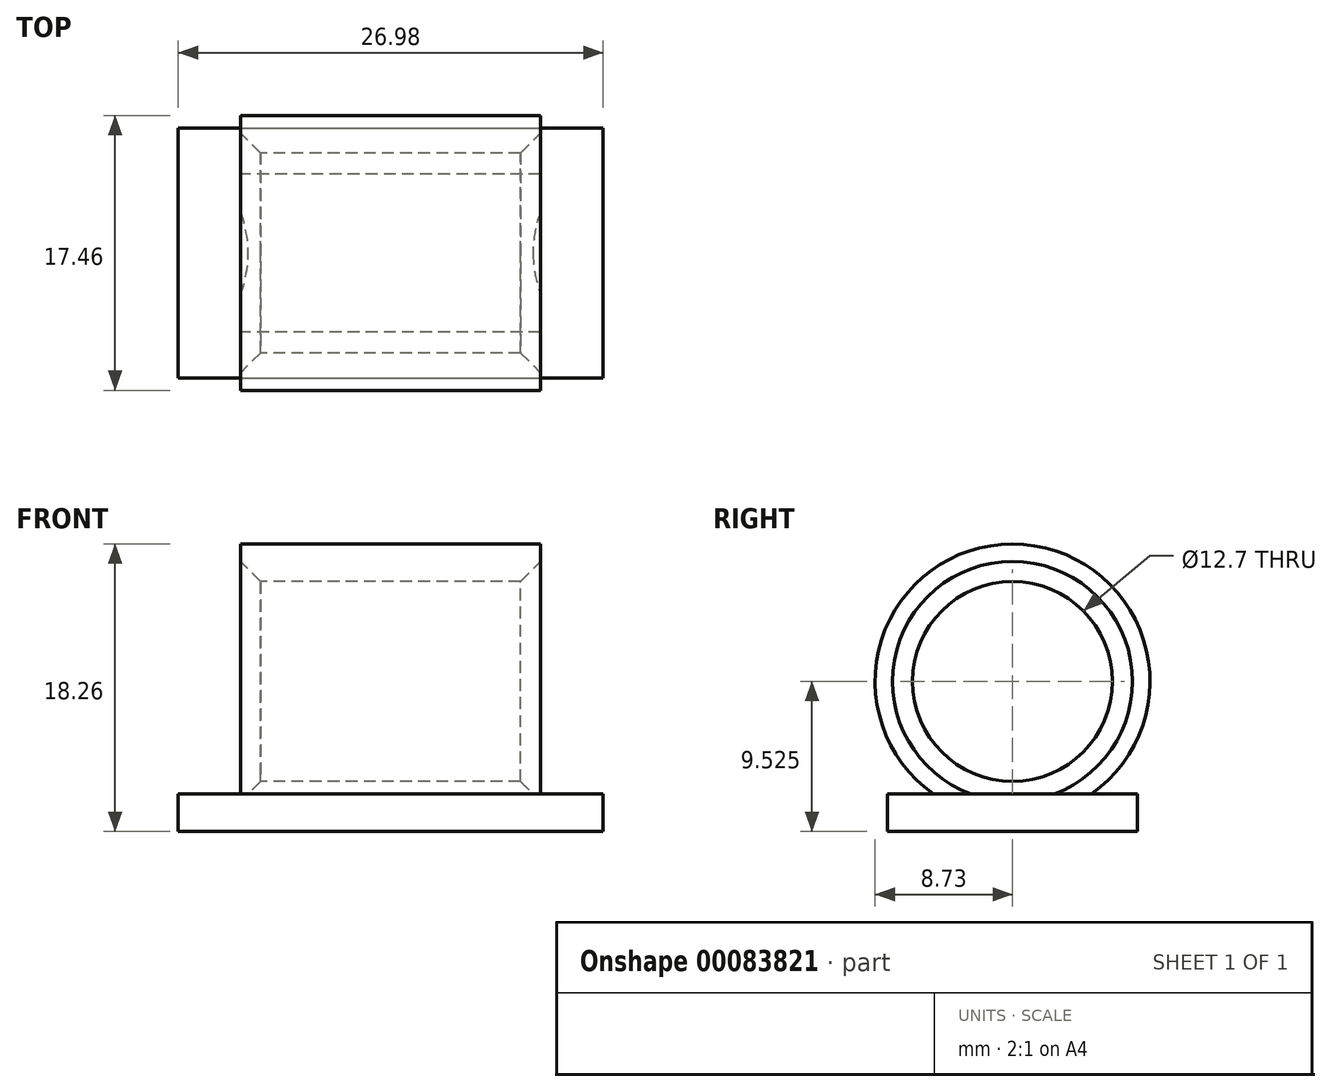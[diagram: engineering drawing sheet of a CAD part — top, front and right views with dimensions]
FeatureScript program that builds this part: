
annotation { "Feature Type Name" : "Feature", "Feature Type Description" : "" }
export const myFeature = defineFeature(function(context is Context, id is Id, definition is map)
    precondition{}
    {
        {
            var Q0;
            Q0=qCreatedBy(makeId("Top.planeOp"),FACE);
            var sketch = newSketch(context, id + "F0", { "sketchPlane" : qUnion([Q0])});
            skLineSegment(sketch, "E0.bottom", {"start": v(-13.5, 7.94) * mm, "end": v(13.5, 7.94) * mm});
            skLineSegment(sketch, "E0.top", {"start": v(-13.5, -7.94) * mm, "end": v(13.5, -7.94) * mm});
            skLineSegment(sketch, "E0.left", {"start": v(-13.5, 7.94) * mm, "end": v(-13.5, -7.94) * mm});
            skLineSegment(sketch, "E0.right", {"start": v(13.5, 7.94) * mm, "end": v(13.5, -7.94) * mm});
            skSolve(sketch);
        }
        {
            var Q0;
            Q0=makeQuery(id+"F0.imprint","IMPRINT",FACE,{"disambiguationData":[TD([[makeQuery(id+"F0.imprint","IMPRINT",EDGE,{"derivedFrom":sQuery(id+"F0.wireOp",EDGE,"E0.bottom")}),-1.0]])]});
            extrude(context, id + "F1", {"entities" : qUnion([Q0]), "depth" : 2.38 * mm});
        }
        {
            var Q0;
            Q0=qCreatedBy(makeId("Right.planeOp"),FACE);
            var sketch = newSketch(context, id + "F2", { "sketchPlane" : qUnion([Q0])});
            skCircle(sketch, "E1", {"center": v(0, 9.53) * mm, "radius": 6.35 * mm});
            skCircle(sketch, "E2", {"center": v(0, 9.53) * mm, "radius": 8.73 * mm});
            skLineSegment(sketch, "E3.0", {"start": v(7.94, 2.38) * mm, "end": v(-7.94, 2.38) * mm});
            skSolve(sketch);
        }
        {
            var Q0;
            Q0=makeQuery(id+"F2.imprint","IMPRINT",FACE,{"disambiguationData":[TD([[makeQuery(id+"F2.imprint","IMPRINT",EDGE,{"derivedFrom":sQuery(id+"F2.wireOp",EDGE,"E1")}),-1.0]])]});
            extrude(context, id + "F3", {"entities" : qUnion([Q0]), "operationType" : NewBodyOperationType.ADD, "endBound" : BoundingType.SYMMETRIC, "depth" : 19.05 * mm});
        }
        {
            var Q0;
            Q0=makeQuery(id+"F3.opExtrude","CAP_EDGE",EDGE,{"disambiguationData":[OSD([sQuery(id+"F2.wireOp",EDGE,"E1")])],"isStart":false});
            var Q1;
            Q1=makeQuery(id+"F3.opExtrude","CAP_EDGE",EDGE,{"disambiguationData":[OSD([sQuery(id+"F2.wireOp",EDGE,"E1")])],"isStart":true});
            chamfer(context, id + "F4", {"entities" : qUnion([Q0, Q1]), "width" : 1.27 * mm, "tangentPropagation" : true});
        }
    });
